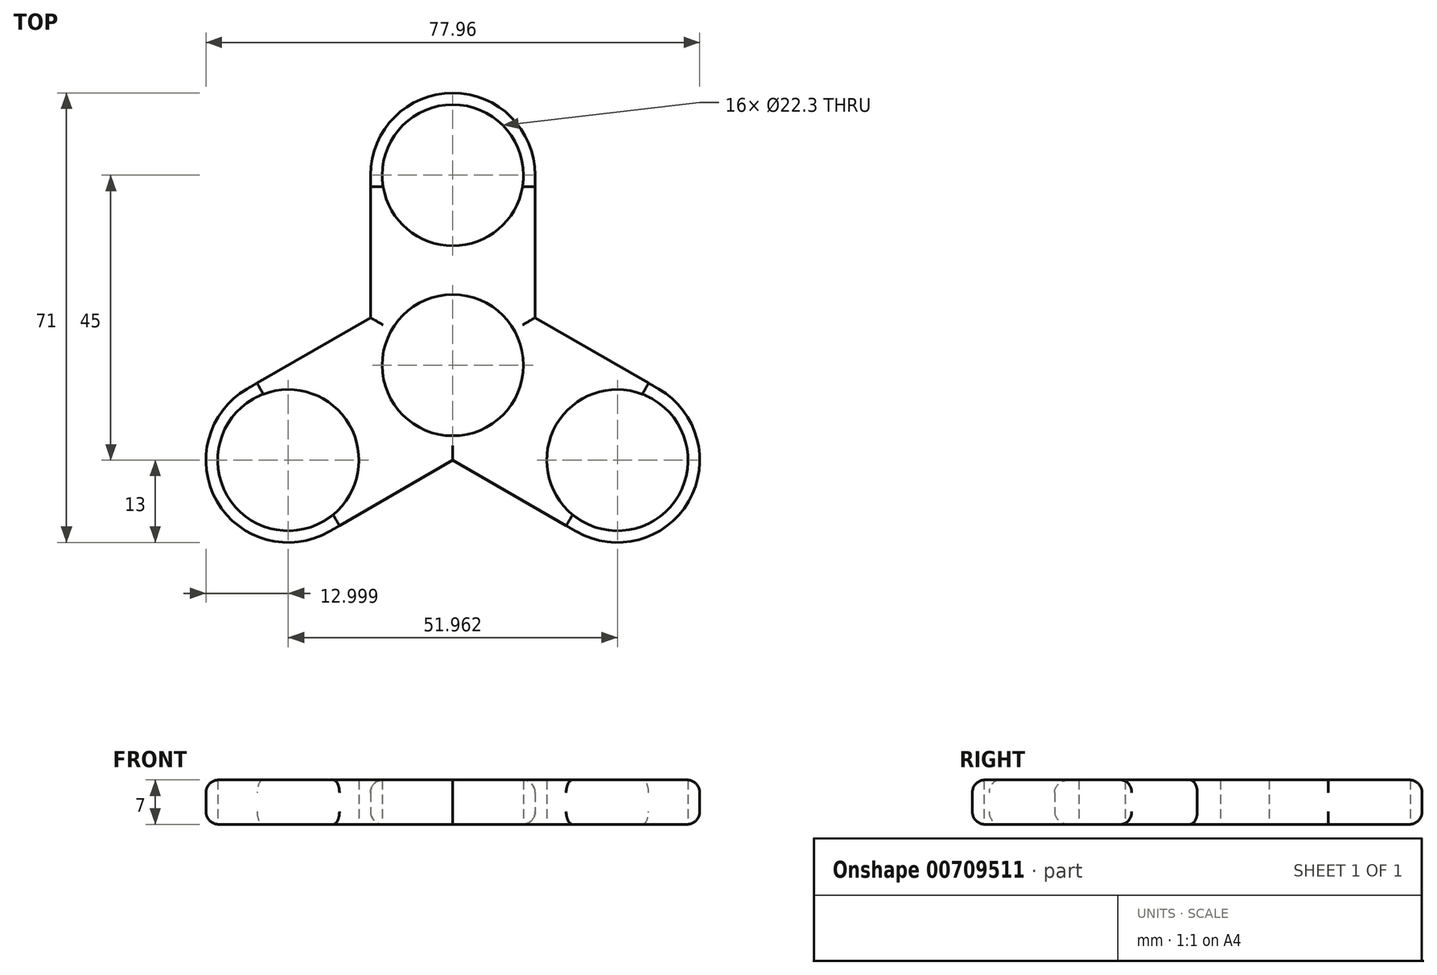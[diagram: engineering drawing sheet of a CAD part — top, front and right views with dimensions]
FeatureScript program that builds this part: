
annotation { "Feature Type Name" : "Feature", "Feature Type Description" : "" }
export const myFeature = defineFeature(function(context is Context, id is Id, definition is map)
    precondition{}
    {
        {
            var Q0;
            Q0=qCreatedBy(makeId("Top.planeOp"),FACE);
            var sketch = newSketch(context, id + "F0", { "sketchPlane" : qUnion([Q0])});
            skCircle(sketch, "E0", {"center": v(0, 0) * mm, "radius": 11.15 * mm});
            skCircle(sketch, "E1", {"center": v(0, 0) * mm, "radius": 13 * mm});
            skCircle(sketch, "E2", {"center": v(0, 30) * mm, "radius": 11.15 * mm});
            skCircle(sketch, "E3", {"center": v(0, 30) * mm, "radius": 13 * mm});
            skLineSegment(sketch, "E4", {"start": v(-13, 30) * mm, "end": v(-13, 0) * mm});
            skLineSegment(sketch, "E5", {"start": v(13, 30) * mm, "end": v(13, 0) * mm});
            skCircle(sketch, "E6.1.0", {"center": v(-25.98, -15) * mm, "radius": 13 * mm});
            skLineSegment(sketch, "E6.1.1", {"start": v(-19.48, -26.26) * mm, "end": v(6.5, -11.26) * mm});
            skLineSegment(sketch, "E6.1.2", {"start": v(-32.48, -3.74) * mm, "end": v(-6.5, 11.26) * mm});
            skCircle(sketch, "E6.1.3", {"center": v(-25.98, -15) * mm, "radius": 11.15 * mm});
            skCircle(sketch, "E6.2.0", {"center": v(25.98, -15) * mm, "radius": 13 * mm});
            skLineSegment(sketch, "E6.2.1", {"start": v(32.48, -3.74) * mm, "end": v(6.5, 11.26) * mm});
            skLineSegment(sketch, "E6.2.2", {"start": v(19.48, -26.26) * mm, "end": v(-6.5, -11.26) * mm});
            skCircle(sketch, "E6.2.3", {"center": v(25.98, -15) * mm, "radius": 11.15 * mm});
            skSolve(sketch);
        }
        {
            var Q0;
            Q0=makeQuery(id+"F0.imprint","IMPRINT",FACE,{"disambiguationData":[TD([[makeQuery(id+"F0.imprint","IMPRINT",EDGE,{"derivedFrom":sQuery(id+"F0.wireOp",EDGE,"E6.2.3")}),-1.0]])]});
            var Q1;
            {var subQ5=sQuery(id+"F0.wireOp",EDGE,"E1");var subQ9=sQuery(id+"F0.wireOp",EDGE,"E5");var subQ11=makeQuery(id+"F0.imprint","INTERSECT",VERTEX,{"derivedFrom":[subQ9,subQ5]});Q1=makeQuery(id+"F0.imprint","IMPRINT",FACE,{"disambiguationData":[TD([[makeQuery(id+"F0.imprint","IMPRINT",EDGE,{"disambiguationData":[TD([[subQ11,1.0]])],"derivedFrom":subQ9}),1.0]])]});}
            var Q2;
            {var subQ0=sQuery(id+"F0.wireOp",EDGE,"E1");var subQ1=sQuery(id+"F0.wireOp",EDGE,"E6.1.1");var subQ2=makeQuery(id+"F0.imprint","INTERSECT",VERTEX,{"derivedFrom":[subQ1,subQ0]});Q2=makeQuery(id+"F0.imprint","IMPRINT",FACE,{"disambiguationData":[TD([[makeQuery(id+"F0.imprint","IMPRINT",EDGE,{"disambiguationData":[TD([[subQ2,1.0]])],"derivedFrom":subQ1}),1.0]])]});}
            var Q3;
            {var subQ0=sQuery(id+"F0.wireOp",EDGE,"E1");var subQ1=sQuery(id+"F0.wireOp",EDGE,"E4");var subQ2=makeQuery(id+"F0.imprint","INTERSECT",VERTEX,{"derivedFrom":[subQ1,subQ0]});Q3=makeQuery(id+"F0.imprint","IMPRINT",FACE,{"disambiguationData":[TD([[makeQuery(id+"F0.imprint","IMPRINT",EDGE,{"disambiguationData":[TD([[subQ2,1.0]])],"derivedFrom":subQ1}),1.0]])]});}
            var Q4;
            {var subQ0=sQuery(id+"F0.wireOp",EDGE,"E1");var subQ1=sQuery(id+"F0.wireOp",EDGE,"E5");var subQ2=makeQuery(id+"F0.imprint","INTERSECT",VERTEX,{"derivedFrom":[subQ1,subQ0]});Q4=makeQuery(id+"F0.imprint","IMPRINT",FACE,{"disambiguationData":[TD([[makeQuery(id+"F0.imprint","IMPRINT",EDGE,{"disambiguationData":[TD([[subQ2,1.0]])],"derivedFrom":subQ1}),-1.0]])]});}
            var Q5;
            Q5=makeQuery(id+"F0.imprint","IMPRINT",FACE,{"disambiguationData":[TD([[makeQuery(id+"F0.imprint","IMPRINT",EDGE,{"derivedFrom":sQuery(id+"F0.wireOp",EDGE,"E0")}),-1.0]])]});
            var Q6;
            Q6=makeQuery(id+"F0.imprint","IMPRINT",FACE,{"disambiguationData":[TD([[makeQuery(id+"F0.imprint","IMPRINT",EDGE,{"derivedFrom":sQuery(id+"F0.wireOp",EDGE,"E6.1.3")}),-1.0]])]});
            var Q7;
            {var subQ3=sQuery(id+"F0.wireOp",EDGE,"E4");var subQ7=sQuery(id+"F0.wireOp",EDGE,"E1");var subQ11=makeQuery(id+"F0.imprint","INTERSECT",VERTEX,{"derivedFrom":[subQ3,subQ7]});Q7=makeQuery(id+"F0.imprint","IMPRINT",FACE,{"disambiguationData":[TD([[makeQuery(id+"F0.imprint","IMPRINT",EDGE,{"disambiguationData":[TD([[subQ11,1.0]])],"derivedFrom":subQ3}),-1.0]])]});}
            var Q8;
            Q8=makeQuery(id+"F0.imprint","IMPRINT",FACE,{"disambiguationData":[TD([[makeQuery(id+"F0.imprint","IMPRINT",EDGE,{"derivedFrom":sQuery(id+"F0.wireOp",EDGE,"E2")}),-1.0]])]});
            var Q9;
            {var subQ1=sQuery(id+"F0.wireOp",EDGE,"E3");var subQ5=sQuery(id+"F0.wireOp",EDGE,"E4");var subQ6=makeQuery(id+"F0.imprint","INTERSECT",VERTEX,{"derivedFrom":[subQ1,subQ5]});Q9=makeQuery(id+"F0.imprint","IMPRINT",FACE,{"disambiguationData":[TD([[makeQuery(id+"F0.imprint","IMPRINT",EDGE,{"disambiguationData":[TD([[subQ6,-1.0]])],"derivedFrom":subQ1}),-1.0]])]});}
            extrude(context, id + "F1", {"entities" : qUnion([Q0, Q1, Q2, Q3, Q4, Q5, Q6, Q7, Q8, Q9]), "depth" : 7 * mm, "offsetDistance" : 25 * mm});
        }
        {
            var Q0;
            Q0=makeQuery(id+"F1.opExtrude","CAP_EDGE",EDGE,{"disambiguationData":[OSD([sQuery(id+"F0.wireOp",EDGE,"E6.2.1")])],"isStart":false});
            var Q1;
            Q1=makeQuery(id+"F1.opExtrude","CAP_EDGE",EDGE,{"disambiguationData":[OSD([sQuery(id+"F0.wireOp",EDGE,"E6.2.0")])],"isStart":false});
            var Q2;
            Q2=makeQuery(id+"F1.opExtrude","CAP_EDGE",EDGE,{"disambiguationData":[OSD([sQuery(id+"F0.wireOp",EDGE,"E6.2.0")])],"isStart":true});
            var Q3;
            Q3=makeQuery(id+"F1.opExtrude","CAP_EDGE",EDGE,{"disambiguationData":[OSD([sQuery(id+"F0.wireOp",EDGE,"E6.2.1")])],"isStart":true});
            var Q4;
            Q4=makeQuery(id+"F1.opExtrude","CAP_EDGE",EDGE,{"disambiguationData":[OSD([sQuery(id+"F0.wireOp",EDGE,"E5")])],"isStart":false});
            var Q5;
            Q5=makeQuery(id+"F1.opExtrude","CAP_EDGE",EDGE,{"disambiguationData":[OSD([sQuery(id+"F0.wireOp",EDGE,"E5")])],"isStart":true});
            var Q6;
            Q6=makeQuery(id+"F1.opExtrude","CAP_EDGE",EDGE,{"disambiguationData":[OSD([sQuery(id+"F0.wireOp",EDGE,"E6.1.2")])],"isStart":false});
            var Q7;
            Q7=makeQuery(id+"F1.opExtrude","CAP_EDGE",EDGE,{"disambiguationData":[OSD([sQuery(id+"F0.wireOp",EDGE,"E6.1.2")])],"isStart":true});
            fillet(context, id + "F2", {"entities" : qUnion([Q0, Q1, Q2, Q3, Q4, Q5, Q6, Q7]), "radius" : 2 * mm, "tangentPropagation" : true, "allowEdgeOverflow" : false});
        }
    });
